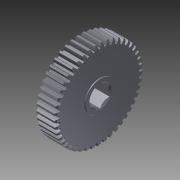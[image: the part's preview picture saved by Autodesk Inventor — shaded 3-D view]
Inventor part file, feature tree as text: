
AUTODESK INVENTOR PART (.ipt)
format: ipt  version: 2014 SP1 (Build 180222100, 222)  size: 540,160 bytes
history: native  units: mm (DEFAULTED — no unit token found)
features: extrude x4, sketch x4, chamfer x3, other x1, fillet x1
ambient origin geometry x8: Origin, YZ Plane, XZ Plane, XY Plane, X Axis, Y Axis, Z Axis, Center Point
bodies: Solid1 (feature_tree)
feature tree (13):
  other  "Gear Blank"
  extrude  "Tooth Profile"  Depth=55.329638mm
  chamfer  "Bore Chamfer Interior"  Distance=28.575mm
  extrude  "Hub"  Depth=12.7mm
  fillet  "Hub Fillet"  Radius=25.4mm
  chamfer  "Bore Chamfer Exterior"  Distance=450.0mm
  chamfer  "Bore Chamfer on Hub"  Distance=1.27mm
  extrude  "Hex Broach"  Depth=12.7mm
  extrude  "Key"  Depth=12.7mm
  sketch  "Sketch2"  dims[d12=90.0deg d24=55.329638mm]
  sketch  "Sketch3"  dims[d26=0.0mm]
  sketch  "Sketch5"  dims[d31=20.32mm]
  sketch  "Sketch16"  dims[d32=0.762mm d77=28.575mm d78=12.7mm d79=25.4mm d83=450.0mm d95=1.27mm d96=3.175mm d97=1.27mm d98=3.175mm d99=1.27mm d100=3.175mm d104=29.845mm d108=30.0deg d109=30.0deg d110=13.5382mm d112=0.254mm d117=2.38125mm d118=5.159375mm d119=25.4mm d120=0.0mm d121=45.0deg d122=45.0deg d123=45.0deg]
